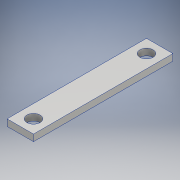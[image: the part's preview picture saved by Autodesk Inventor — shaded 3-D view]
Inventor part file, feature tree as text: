
AUTODESK INVENTOR PART (.ipt)
format: ipt  version: 2018.1 (Build 221171000, 171)  size: 102,912 bytes
history: native  units: mm
features: other x1, extrude x1, sketch x1
ambient origin geometry x8: Origin, YZ Plane, XZ Plane, XY Plane, X Axis, Y Axis, Z Axis, Center Point
bodies: Body1 (feature_tree)
feature tree (3):
  other  "ソリッド1"
  extrude  "押し出し1"  Depth=20.0mm
  sketch  "スケッチ1"
